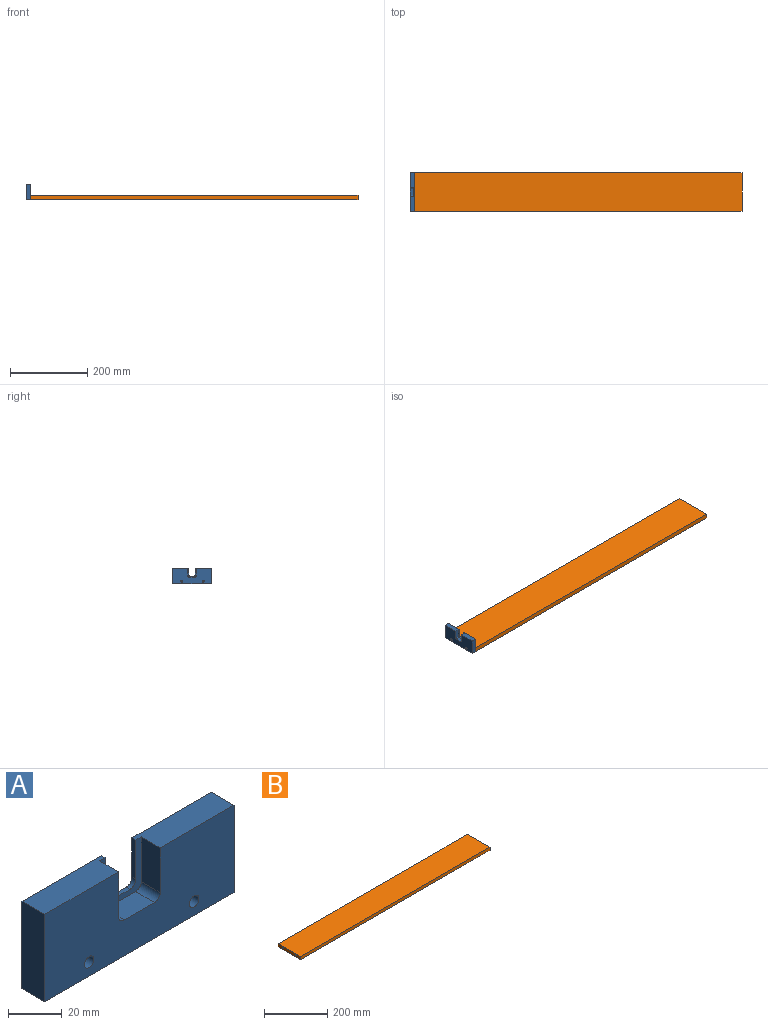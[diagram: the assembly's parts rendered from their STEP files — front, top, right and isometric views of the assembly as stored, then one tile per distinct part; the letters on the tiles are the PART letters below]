
ASSEMBLY  parts=2 mates=1
PART A: 20 faces, bbox 100x12x40 mm
  f0: plane 41.9x12mm, normal (0,0,1), area 473.8mm2, adj f1,f2,f5,f6,f10,f15
  f1: plane 100x40mm, normal (0,1,0), area 3624.4mm2, adj f0,f3,f4,f6,f7,f8,f9,f15
  f2: plane 23.5x22mm, normal (0,-1,0), area 176.8mm2, adj f0,f3,f10,f11,f12,f13,f14,f15
  f3: plane 41.9x12mm, normal (0,0,1), area 473.8mm2, adj f1,f2,f4,f5,f11,f16
  f4: plane 40x12mm, normal (-1,0,0), area 480mm2, adj f1,f3,f5,f7
  f5: plane 100x40mm, normal (0,-1,0), area 3447.6mm2, adj f0,f3,f4,f6,f7,f8,f9,f10
  f6: plane 40x12mm, normal (1,0,0), area 480mm2, adj f0,f1,f5,f7
  f7: plane 100x12mm, normal (0,0,-1), area 1200mm2, adj f1,f4,f5,f6
  f8: cylinder r=2.5mm len=12mm, axis (0,-1,0), area 188.5mm2, adj f1,f5
  f9: cylinder r=2.5mm len=12mm, axis (0,-1,0), area 188.5mm2, adj f1,f5
  f10: plane 20.5x10mm, normal (-1,0,0), area 205mm2, adj f0,f2,f5,f14
  f11: plane 20.5x10mm, normal (1,0,0), area 205mm2, adj f2,f3,f5,f12
  f12: cylinder r=3mm len=10mm, axis (0,-1,0), area 47.1mm2, adj f2,f5,f11,f13
  f13: plane 16x10mm, normal (0,0,1), area 160mm2, adj f2,f5,f12,f14
  f14: cylinder r=3mm len=10mm, axis (0,-1,0), area 47.1mm2, adj f2,f5,f10,f13
  f15: plane 18x2mm, normal (-1,0,0), area 36mm2, adj f0,f1,f2,f19
  f16: plane 18x2mm, normal (1,0,0), area 36mm2, adj f1,f2,f3,f17
  f17: cylinder r=3mm len=3mm, axis (0,-1,0), area 9.4mm2, adj f1,f2,f16,f18
  f18: plane 10.2x2mm, normal (0,0,1), area 20.4mm2, adj f1,f2,f17,f19
  f19: cylinder r=3mm len=3mm, axis (0,-1,0), area 9.4mm2, adj f1,f2,f15,f18
PART B: 10 faces, bbox 850x100x12 mm
  f0: plane 100x12mm, normal (-1,0,0), area 1168.2mm2, adj f1,f3,f4,f5,f6,f8
  f1: plane 850x12mm, normal (0,-1,0), area 10200mm2, adj f0,f2,f4,f5
  f2: plane 100x12mm, normal (1,0,0), area 1200mm2, adj f1,f3,f4,f5
  f3: plane 850x12mm, normal (0,1,0), area 10200mm2, adj f0,f2,f4,f5
  f4: plane 850x100mm, normal (0,0,1), area 85000mm2, adj f0,f1,f2,f3
  f5: plane 850x100mm, normal (0,0,-1), area 85000mm2, adj f0,f1,f2,f3
  f6: cylinder r=2.25mm len=15mm, axis (-1,0,0), area 212.1mm2, adj f0,f7
  f7: cone r=0mm half-angle=59deg, axis (-1,0,0), area 18.6mm2, adj f6
  f8: cylinder r=2.25mm len=15mm, axis (-1,0,0), area 212.1mm2, adj f0,f9
  f9: cone r=0mm half-angle=59deg, axis (-1,0,0), area 18.6mm2, adj f8
PLACE A rot(axis=(0,0,-1),90deg) t=(-223.85,160.05,-169.45)mm
PLACE B t=(-223.85,160.05,-169.45)mm
MATE revolute A.f9 <-> B.f8  axis (1,0,0) through (-223.85,81.05,-162.95)mm
